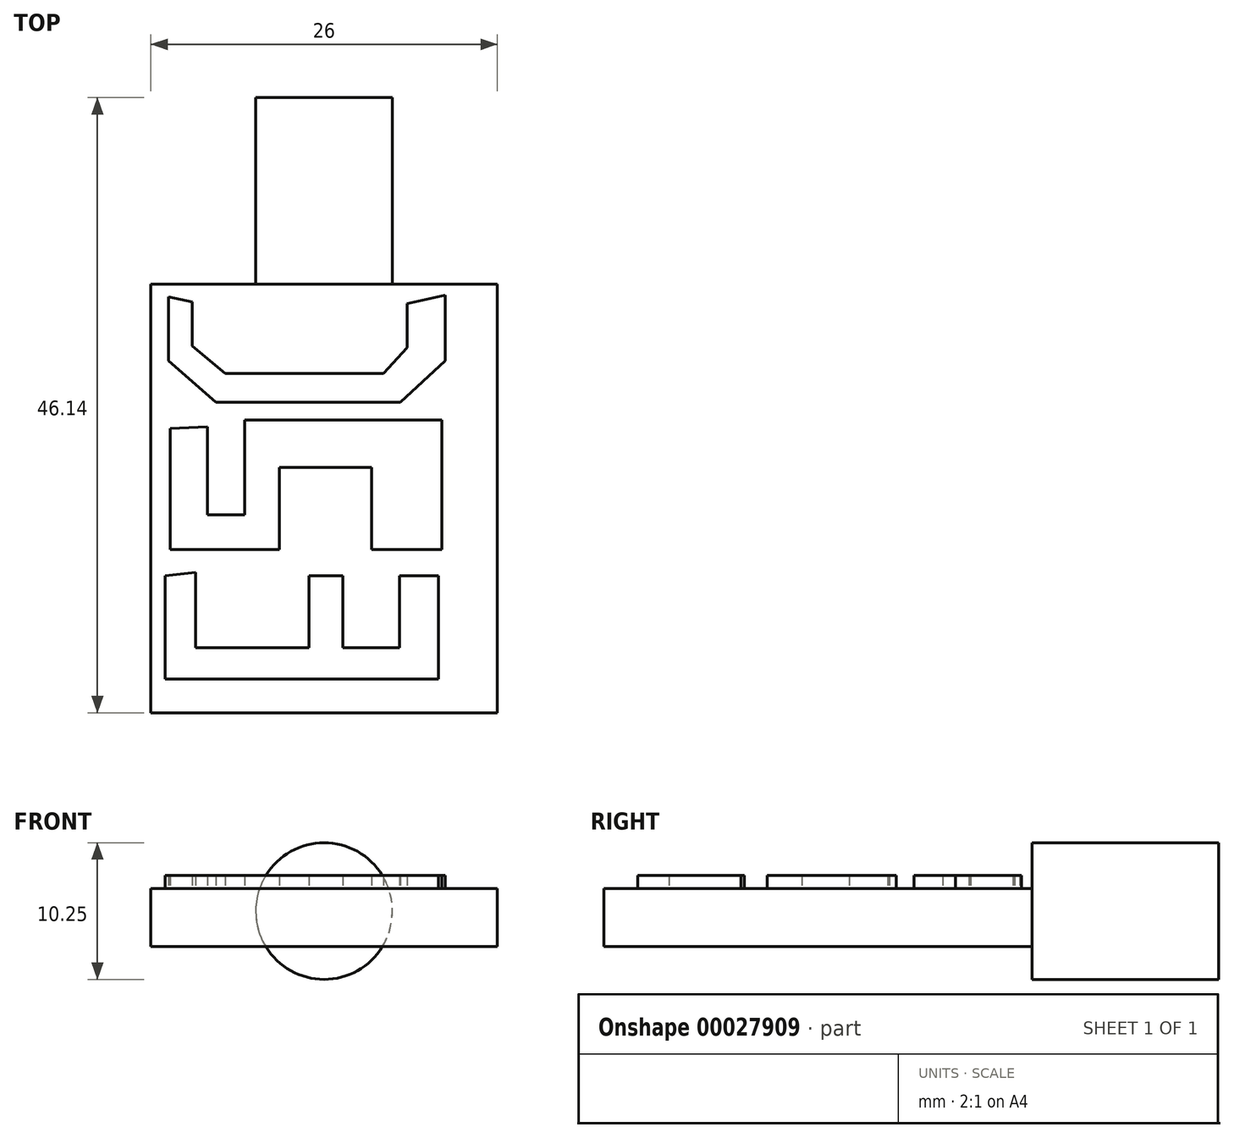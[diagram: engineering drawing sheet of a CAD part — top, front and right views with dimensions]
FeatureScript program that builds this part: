
annotation { "Feature Type Name" : "Feature", "Feature Type Description" : "" }
export const myFeature = defineFeature(function(context is Context, id is Id, definition is map)
    precondition{}
    {
        {
            var Q0;
            Q0=qCreatedBy(makeId("Top.planeOp"),FACE);
            var sketch = newSketch(context, id + "F0", { "sketchPlane" : qUnion([Q0])});
            skLineSegment(sketch, "E0.rect.bottom", {"start": v(13, 16.07) * mm, "end": v(-13, 16.07) * mm});
            skLineSegment(sketch, "E0.rect.top", {"start": v(13, -16.07) * mm, "end": v(-13, -16.07) * mm});
            skLineSegment(sketch, "E0.rect.left", {"start": v(13, 16.07) * mm, "end": v(13, -16.07) * mm});
            skLineSegment(sketch, "E0.rect.right", {"start": v(-13, 16.07) * mm, "end": v(-13, -16.07) * mm});
            skPoint(sketch, "E0.rect.middle", {"position": v(0, 0) * mm});
            skSolve(sketch);
        }
        {
            var Q0;
            Q0 = qSketchRegion(id + "F0", true);
            extrude(context, id + "F1", {"entities" : qUnion([Q0]), "depth" : 4.35 * mm});
        }
        {
            var Q0;
            Q0=makeQuery(id+"F1.opExtrude","SWEPT_FACE",FACE,{"disambiguationData":[OSD([sQuery(id+"F0.wireOp",EDGE,"E0.rect.bottom")])]});
            var sketch = newSketch(context, id + "F2", { "sketchPlane" : qUnion([Q0])});
            skCircle(sketch, "E1", {"center": v(0, 2.67) * mm, "radius": 5.13 * mm});
            skPoint(sketch, "E1.centerSnap0", {"position": v(0, 4.35) * mm});
            skSolve(sketch);
        }
        {
            var Q0;
            {var subQ0=makeQuery(id+"F1.opExtrude","CAP_EDGE",EDGE,{"disambiguationData":[OSD([sQuery(id+"F0.wireOp",EDGE,"E0.rect.bottom")])],"isStart":false});var subQ1=sQuery(id+"F2.wireOp",EDGE,"E1");var subQ3=makeQuery(id+"F2.imprint","INTERSECT",VERTEX,{"disambiguationData":[OD(0.0)],"derivedFrom":[subQ0,subQ1]});Q0=makeQuery(id+"F2.imprint","IMPRINT",FACE,{"disambiguationData":[TD([[makeQuery(id+"F2.imprint","IMPRINT",EDGE,{"disambiguationData":[TD([[subQ3,1.0]])],"derivedFrom":subQ1}),1.0]])]});}
            var Q1;
            {var subQ0=sQuery(id+"F0.wireOp",EDGE,"E0.rect.bottom");var subQ1=makeQuery(id+"F1.opExtrude","CAP_EDGE",EDGE,{"disambiguationData":[OSD([subQ0])],"isStart":false});var subQ2=sQuery(id+"F2.wireOp",EDGE,"E1");var subQ4=makeQuery(id+"F2.imprint","INTERSECT",VERTEX,{"disambiguationData":[OD(0.0)],"derivedFrom":[subQ1,subQ2]});Q1=makeQuery(id+"F2.imprint","IMPRINT",FACE,{"disambiguationData":[TD([[makeQuery(id+"F2.imprint","IMPRINT",EDGE,{"disambiguationData":[TD([[subQ4,-1.0]])],"derivedFrom":subQ2}),1.0]])]});}
            var Q2;
            {var subQ0=makeQuery(id+"F1.opExtrude","CAP_EDGE",EDGE,{"disambiguationData":[OSD([sQuery(id+"F0.wireOp",EDGE,"E0.rect.bottom")])],"isStart":true});var subQ1=sQuery(id+"F2.wireOp",EDGE,"E1");var subQ3=makeQuery(id+"F2.imprint","INTERSECT",VERTEX,{"disambiguationData":[OD(0.0)],"derivedFrom":[subQ0,subQ1]});Q2=makeQuery(id+"F2.imprint","IMPRINT",FACE,{"disambiguationData":[TD([[makeQuery(id+"F2.imprint","IMPRINT",EDGE,{"disambiguationData":[TD([[subQ3,-1.0]])],"derivedFrom":subQ1}),1.0]])]});}
            extrude(context, id + "F3", {"entities" : qUnion([Q0, Q1, Q2]), "operationType" : NewBodyOperationType.ADD, "depth" : 14 * mm});
        }
        {
            var Q0;
            Q0=makeQuery(id+"F1.opExtrude","CAP_FACE",FACE,{"disambiguationData":[OSD([sQuery(id+"F0.wireOp",EDGE,"E0.rect.bottom"),sQuery(id+"F0.wireOp",EDGE,"E0.rect.top"),sQuery(id+"F0.wireOp",EDGE,"E0.rect.left"),sQuery(id+"F0.wireOp",EDGE,"E0.rect.right")])],"isStart":false});
            var sketch = newSketch(context, id + "F4", { "sketchPlane" : qUnion([Q0])});
            skLineSegment(sketch, "E2", {"start": v(-11.91, -5.8) * mm, "end": v(-11.91, -13.53) * mm});
            skLineSegment(sketch, "E3", {"start": v(-11.91, -13.53) * mm, "end": v(8.58, -13.53) * mm});
            skLineSegment(sketch, "E4", {"start": v(8.58, -13.53) * mm, "end": v(8.58, -5.8) * mm});
            skLineSegment(sketch, "E5", {"start": v(8.58, -5.8) * mm, "end": v(5.66, -5.8) * mm});
            skLineSegment(sketch, "E6", {"start": v(5.66, -5.8) * mm, "end": v(5.66, -11.18) * mm});
            skLineSegment(sketch, "E7", {"start": v(5.66, -11.18) * mm, "end": v(1.4, -11.18) * mm});
            skLineSegment(sketch, "E8", {"start": v(1.4, -11.18) * mm, "end": v(1.4, -5.8) * mm});
            skLineSegment(sketch, "E9", {"start": v(1.4, -5.8) * mm, "end": v(-1.13, -5.8) * mm});
            skLineSegment(sketch, "E10", {"start": v(-1.13, -5.8) * mm, "end": v(-1.13, -11.18) * mm});
            skLineSegment(sketch, "E11", {"start": v(-1.13, -11.18) * mm, "end": v(-9.63, -11.18) * mm});
            skLineSegment(sketch, "E12", {"start": v(-9.63, -11.18) * mm, "end": v(-9.63, -5.54) * mm});
            skLineSegment(sketch, "E13", {"start": v(-9.63, -5.54) * mm, "end": v(-11.91, -5.8) * mm});
            skLineSegment(sketch, "E14", {"start": v(-11.53, 5.25) * mm, "end": v(-11.53, -3.83) * mm});
            skLineSegment(sketch, "E15", {"start": v(-11.53, -3.83) * mm, "end": v(-3.35, -3.83) * mm});
            skLineSegment(sketch, "E16", {"start": v(-3.35, -3.83) * mm, "end": v(-3.35, 2.33) * mm});
            skLineSegment(sketch, "E17", {"start": v(-3.35, 2.33) * mm, "end": v(3.56, 2.33) * mm});
            skLineSegment(sketch, "E18", {"start": v(3.56, 2.33) * mm, "end": v(3.56, -3.83) * mm});
            skLineSegment(sketch, "E19", {"start": v(3.56, -3.83) * mm, "end": v(8.83, -3.83) * mm});
            skLineSegment(sketch, "E20", {"start": v(8.83, -3.83) * mm, "end": v(8.83, 5.88) * mm});
            skLineSegment(sketch, "E21", {"start": v(8.83, 5.88) * mm, "end": v(-5.95, 5.88) * mm});
            skLineSegment(sketch, "E22", {"start": v(-5.95, 5.88) * mm, "end": v(-5.95, -1.22) * mm});
            skLineSegment(sketch, "E23", {"start": v(-5.95, -1.22) * mm, "end": v(-8.74, -1.22) * mm});
            skLineSegment(sketch, "E24", {"start": v(-8.74, -1.22) * mm, "end": v(-8.74, 5.37) * mm});
            skLineSegment(sketch, "E25", {"start": v(-8.74, 5.37) * mm, "end": v(-11.53, 5.25) * mm});
            skLineSegment(sketch, "E26", {"start": v(-11.66, 15.14) * mm, "end": v(-11.66, 10.32) * mm});
            skLineSegment(sketch, "E27", {"start": v(-11.66, 10.32) * mm, "end": v(-8.1, 7.21) * mm});
            skLineSegment(sketch, "E28", {"start": v(-8.1, 7.21) * mm, "end": v(5.72, 7.21) * mm});
            skLineSegment(sketch, "E29", {"start": v(5.72, 7.21) * mm, "end": v(9.08, 10.32) * mm});
            skLineSegment(sketch, "E30", {"start": v(9.08, 10.32) * mm, "end": v(9.08, 15.27) * mm});
            skLineSegment(sketch, "E31", {"start": v(9.08, 15.27) * mm, "end": v(6.23, 14.63) * mm});
            skLineSegment(sketch, "E32", {"start": v(6.23, 14.63) * mm, "end": v(6.23, 11.34) * mm});
            skLineSegment(sketch, "E33", {"start": v(6.23, 11.34) * mm, "end": v(4.45, 9.37) * mm});
            skLineSegment(sketch, "E34", {"start": v(4.45, 9.37) * mm, "end": v(-7.4, 9.37) * mm});
            skLineSegment(sketch, "E35", {"start": v(-7.4, 9.37) * mm, "end": v(-9.88, 11.46) * mm});
            skLineSegment(sketch, "E36", {"start": v(-9.88, 11.46) * mm, "end": v(-9.88, 14.76) * mm});
            skLineSegment(sketch, "E37", {"start": v(-9.88, 14.76) * mm, "end": v(-11.66, 15.14) * mm});
            skSolve(sketch);
        }
        {
            var Q0;
            Q0=makeQuery(id+"F4.imprint","IMPRINT",FACE,{"disambiguationData":[TD([[makeQuery(id+"F4.imprint","IMPRINT",EDGE,{"derivedFrom":sQuery(id+"F4.wireOp",EDGE,"E2")}),1.0]])]});
            var Q1;
            Q1=makeQuery(id+"F4.imprint","IMPRINT",FACE,{"disambiguationData":[TD([[makeQuery(id+"F4.imprint","IMPRINT",EDGE,{"derivedFrom":sQuery(id+"F4.wireOp",EDGE,"E14")}),1.0]])]});
            var Q2;
            Q2=makeQuery(id+"F4.imprint","IMPRINT",FACE,{"disambiguationData":[TD([[makeQuery(id+"F4.imprint","IMPRINT",EDGE,{"derivedFrom":sQuery(id+"F4.wireOp",EDGE,"E26")}),1.0]])]});
            extrude(context, id + "F5", {"entities" : qUnion([Q0, Q1, Q2]), "operationType" : NewBodyOperationType.ADD, "depth" : 1 * mm});
        }
    });
